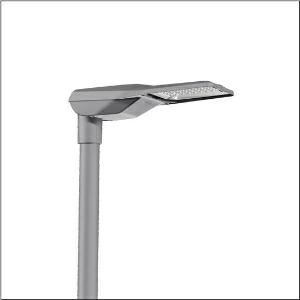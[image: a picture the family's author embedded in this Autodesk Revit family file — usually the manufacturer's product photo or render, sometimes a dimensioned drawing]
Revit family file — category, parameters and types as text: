
# Revit family: streetlight_sl_21_iq_mini___st1_5a_5xe2p41d08hb_72ee
name_source: partatom
category: Lighting Fixtures
units: mm (PartAtom-declared; Revit-internal decimal feet)

## family parameters
Cut with Voids When Loaded = No
Host = Face
Light Source = No
Part Type = Normal
Room Calculation Point = No
Round Connector Dimension = Use Diameter
Shared = No

## types (1)
- --- (1 x LED, 9690 lm, 70.9 W, 4000K)
    Apparent Load = 71 VA
    CIE Flux Codes = 22 53 95 100 100
    Color Rendering = 70
    Color Temperature = 4000K
    Default Elevation = 1800 mm
    Description = Streetlight SL 21 iQ mini, mast luminaire, primary light control with lens, of PMMA, primary optical cover: cover, of toughened safety glass, transparent, light distribution: ST1.5a, light emission: direct distribution, primary light characteristic: asymmetric, installation type: post-top, side-entry, LED, High Power LED, rated luminous flux: 9.690lm, luminous efficacy: 137lm/W, light colour: 740, colour temperature: 4000K, control: Auto-Match, Temp-Guard, Lumen-Switch, Night-Set, Smart-Wire, Light-Fading, Desk-Remote (wireless, voltage-free reading and setting of iQ features in the workshop via application-optimized NFC function/RFID function), optimised constant luminous flux control (CLO 2.0), presetting dimming linear, mains connection: 220..240V, AC, 50/60Hz, start of lifetime: 71W, end of service life: 75W, reduction: 31W, luminaire housing, of diecast aluminium, powder-coated, Siteco® metallic grey (DB 702S), corrosivity category C5 mid according to DIN EN ISO 12944, please order mast flange separately, inclination adjustable: 0°, 5°, 10°, 15°, sealing non-destructively replaceable, multi-level sealing system, length: 628mm, width: 235mm, height: 110mm, mast flange for spigot size: 42mm (side-entry): 5XC10008XM4, 60/48mm (side-entry/post-top): 5XC10108XM2, 76/60mm (side-entry/post-top): 5XC10108XM1, protection rating (complete): IP66, insulation class (complete): insulation class II (safety insulation), certification: CE, ENEC, ENEC+, VDE, impact resistance: IK09, permissible operating ambient temperature for outdoor applications: -40..+50°C, standard-compliant lighting for roads and squares, packaging unit: 1 piece

Light Distribution: ST1.5a
    Height = 110 mm
    Lamp = 1 x LED
    Lamp Light Flux = 9690 lm
    Lamp Power = 70.9 W
    Lamp count = 1
    Length = 625 mm
    Luminous efficacy = 137 lm/W
    Manufacturer = Siteco
    ModVariant = No
    Model = 5XE2P41D08HB
    Number of Poles = 1
    OnlyDefault = Yes
    Power Factor = 1
    Product Name = Streetlight SL 21 iQ mini | ST1.5a
    Product group = mast luminaire | pylon top
    ProductGroupID = 6100
    Protection Class = Protection class II
    Protection Degree = IP 66
    RLX_Detail_Level = 1
    RLX_Emergency_Light_Flux = 0 lm
    RLX_Emergency_Type = 0
    RLX_Emergency_Type_DB = No
    RlxData = <blob elided: 95821 chars, md5=5cf33e8a>
    Socket = socket
    Standby Power = 0 W
    System Light Flux = 9690 lm
    System Power = 71 W
    Type Comments = factory setting: luminous flux: 100 % | dim-lin: 254 | 711 mA
    Type Image = l_1003519.jpg
    URL = http://relux.com
    VarID = @adj_089355
    Voltage = 0 V
    Weight = 0.00 kg
    Width = 234 mm

## geometry (parser evidence)
native form markers: Blend x4, Sweep x9
no freeform markers — native parametric forms only
